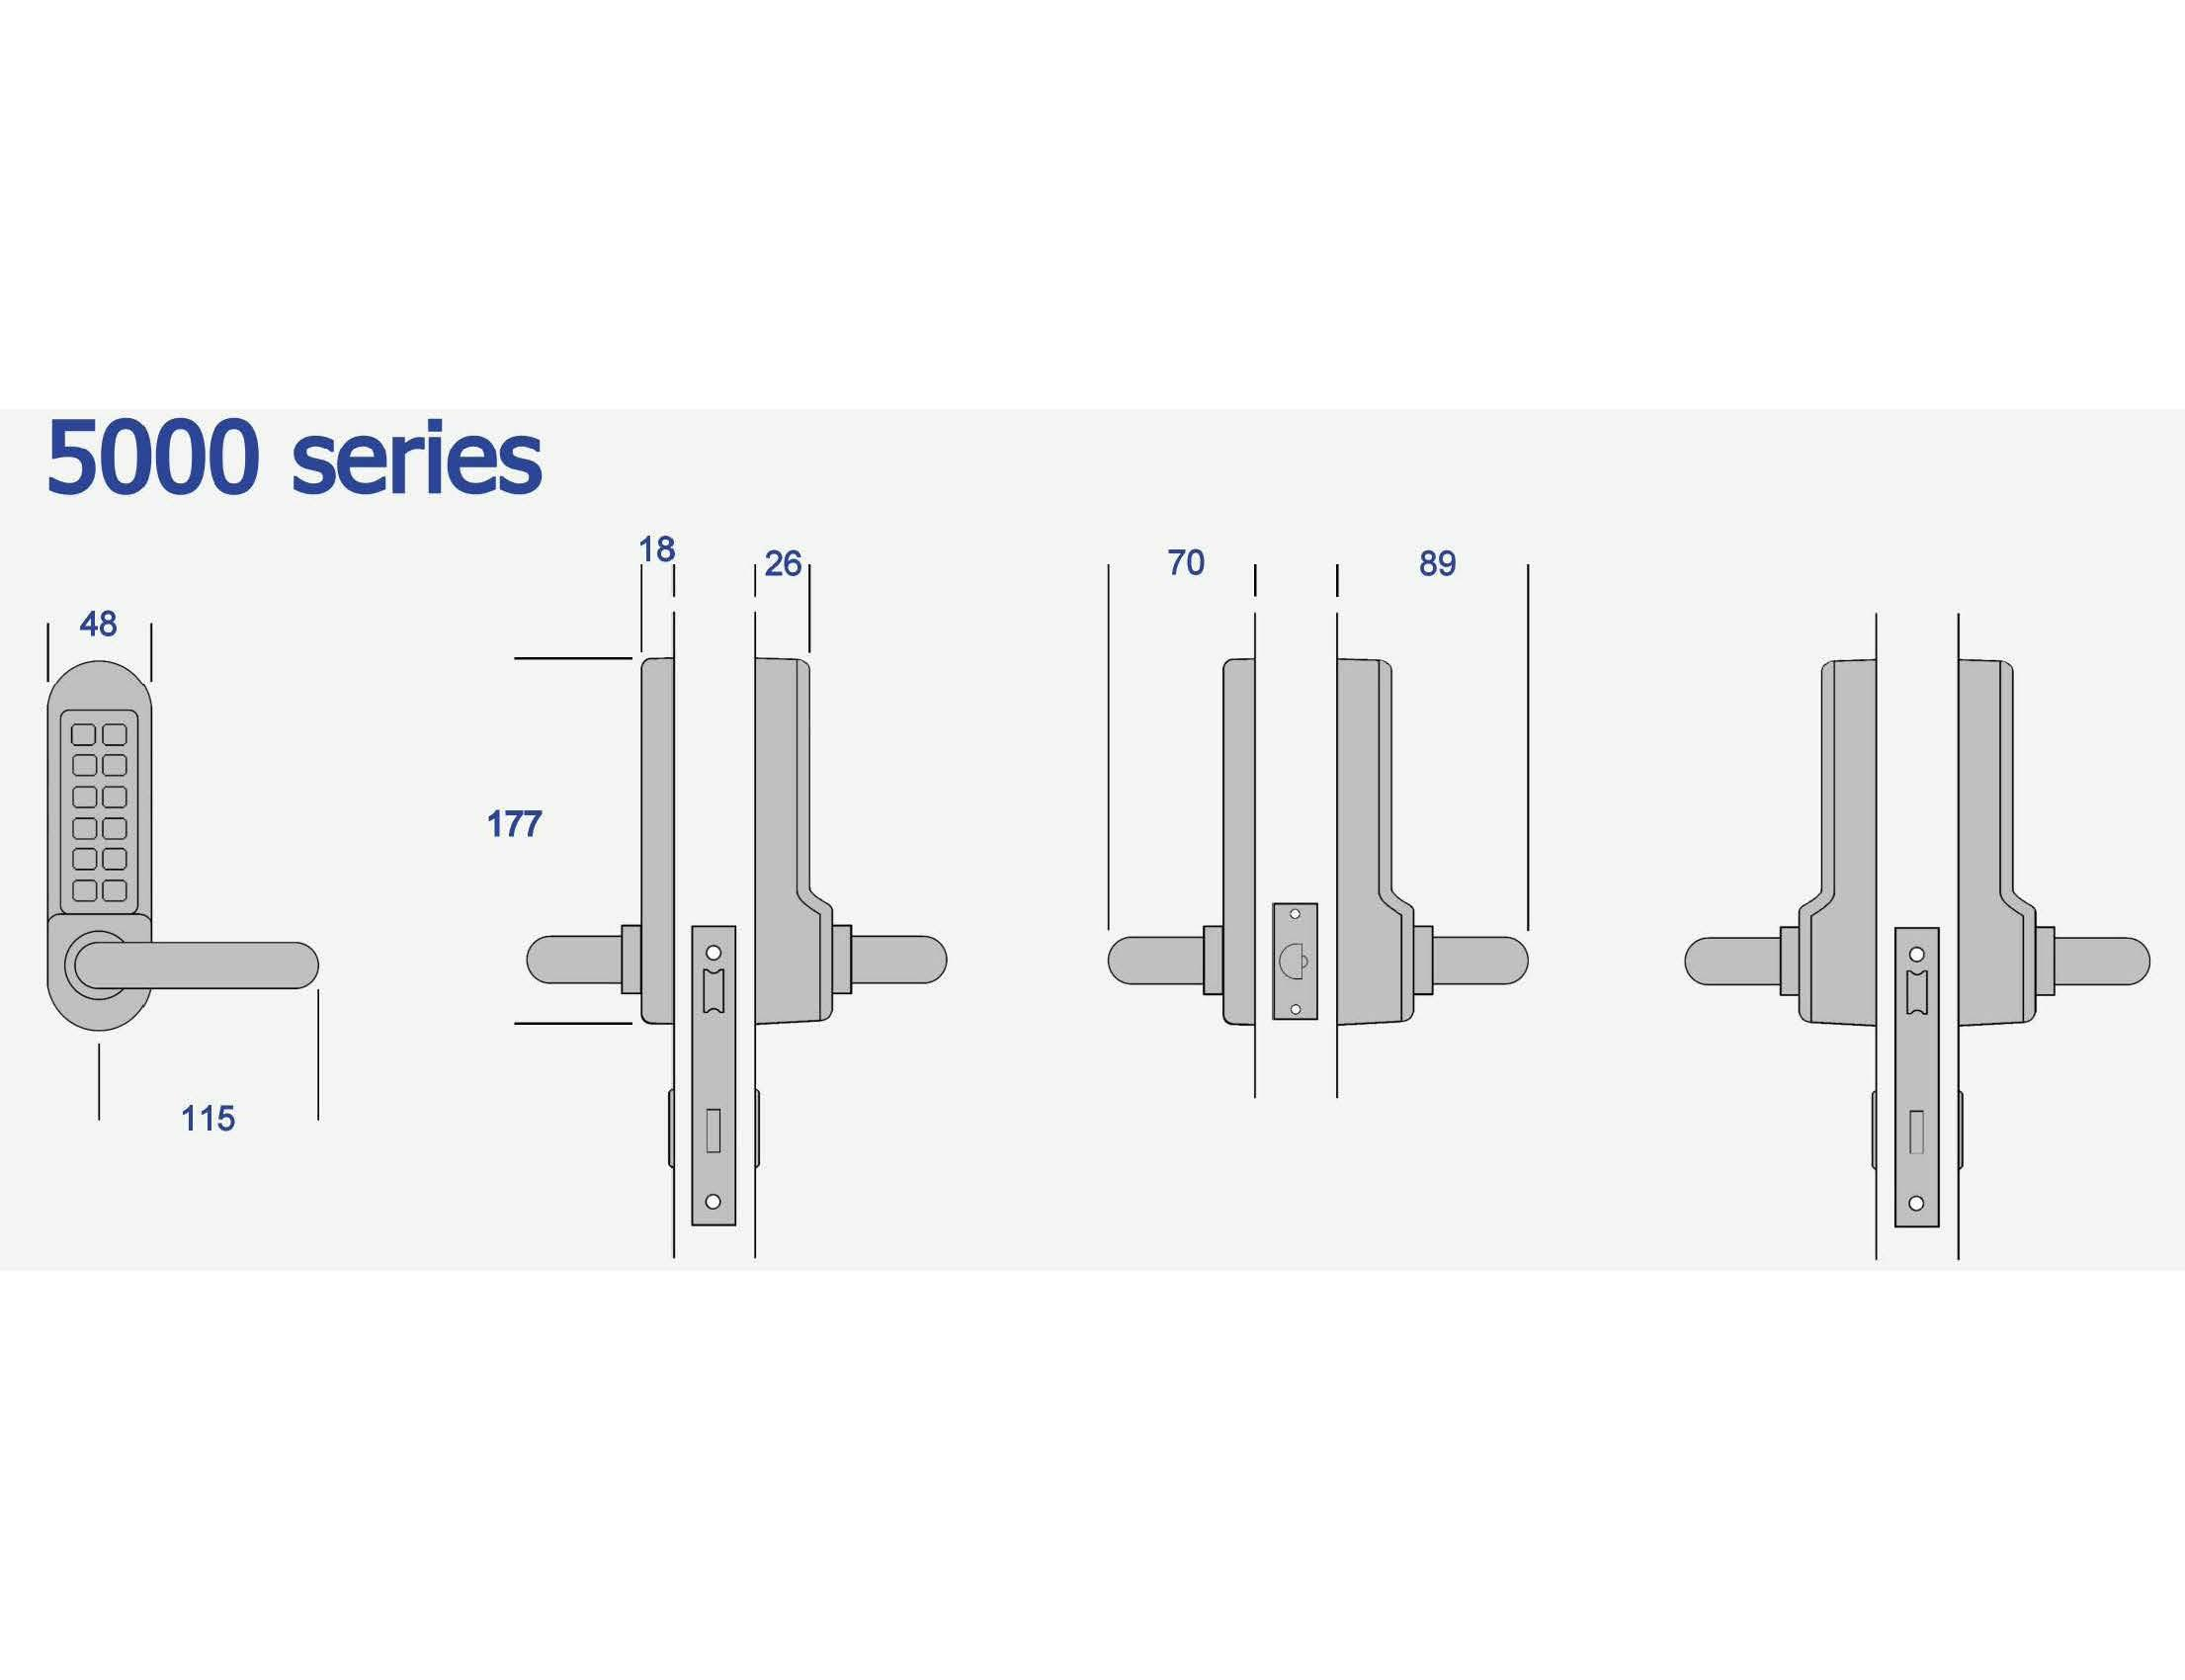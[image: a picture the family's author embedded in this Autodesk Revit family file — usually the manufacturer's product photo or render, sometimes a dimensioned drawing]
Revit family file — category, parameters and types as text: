
# Revit family: NBS_Lomax_Door_FDIN24-14S
name_source: partatom
category: Doors
revit_build: Autodesk Revit Architecture 2016 (Build: 20150220_1215(x64)
units: mm (PartAtom-declared; Revit-internal decimal feet)

## family parameters
Always vertical = Yes
Cut with Voids When Loaded = No
Host = Wall
OmniClass Number = 23.30.10.00
OmniClass Title = Doors
Room Calculation Point = No
Shared = No

## types (1)
- NBS_Lomax_Door_FDIN24-14S
    BIMObjectName = NBS_Lomax_Door_FDIN24-14S
    Category = Doors
    Description = French Doors
    Frame Projection Ext. = 25 mm  [stored 0.082021 ft]
    Frame Projection Int. = 25 mm  [stored 0.082021 ft]
    Frame Width = 76 mm
    Function = Interior
    Glass = Glass
    Height = 2240 mm  [stored 7.34908 ft]
    Higes = Yes
    Hinges = Yes
    Lever Height from FFL = 1000 mm  [stored 3.28084 ft]
    Manufacturer = Lomax
    ManufacturerName = Lomax
    ManufacturerURL = lomaxwood.co.uk
    Model = NBS_Lomax_Door_FDIN24-14S
    ModelNumber = FDIN24-14S
    ModelReference = NBS_Lomax_Door_FDIN24-14S
    NBSDescription = French Doors
    NBSNote = FDIN24-14S
    NBSReference = NBS_Lomax_Door_FDIN24-14S
    Name = FDIN24-14S
    NominalHeight = 2240 mm  [stored 7.34908 ft]
    NominalLength = 76 mm
    NominalWidth = 1480 mm  [stored 4.85564 ft]
    ProductInformation = French Doors
    Revision = 1
    Rough Height = 2240 mm  [stored 7.34908 ft]
    Rough Width = 620 mm
    Thickness = 76 mm
    URL = lomaxwood.co.uk
    Wall Closure = By host
    White = White
    White Wood = WHite Wood
    Width = 1480 mm  [stored 4.85564 ft]
    Wood Wood = Wood Wood

note: [stored X ft] marks values corroborated as IEEE doubles in the binary element streams (Revit-internal decimal feet)

## geometry (parser evidence)
native form markers: Blend x2, Sweep x22
no freeform markers — native parametric forms only
